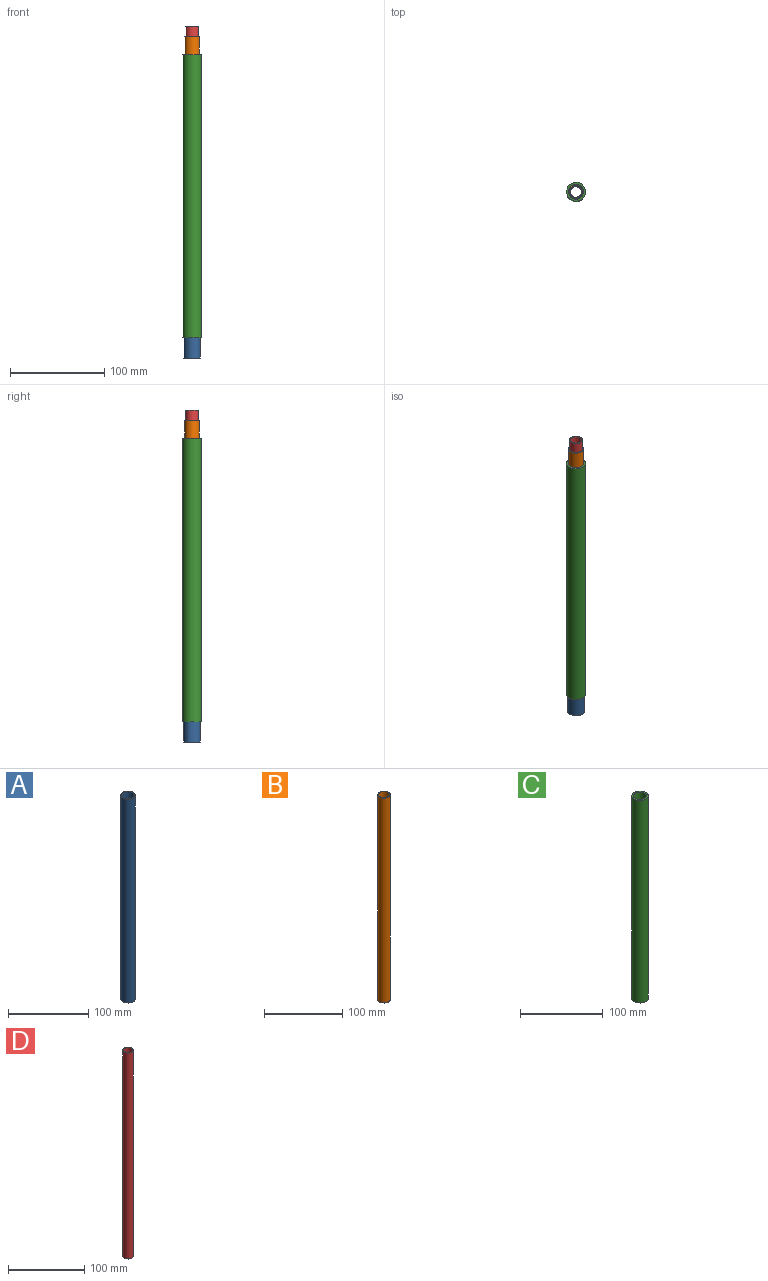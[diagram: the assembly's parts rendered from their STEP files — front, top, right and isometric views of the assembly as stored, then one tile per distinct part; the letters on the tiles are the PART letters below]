
ASSEMBLY  parts=4 mates=3
PART A: 4 faces, bbox 17.9x17.9x310 mm
  f0: cylinder r=7.95mm len=310mm, axis (0,0,-1), area 15484.9mm2, adj f2,f3
  f1: cylinder r=8.95mm len=310mm, axis (0,0,-1), area 17432.7mm2, adj f2,f3
  f2: plane 17.9x17.9mm, normal (0,0,1), area 53.1mm2, adj f0,f1
  f3: plane 17.9x17.9mm, normal (0,0,-1), area 53.1mm2, adj f0,f1
PART B: 4 faces, bbox 15.8x15.8x320 mm
  f0: cylinder r=6.9mm len=320mm, axis (0,0,-1), area 13873.3mm2, adj f2,f3
  f1: cylinder r=7.9mm len=320mm, axis (0,0,-1), area 15883.9mm2, adj f2,f3
  f2: plane 15.8x15.8mm, normal (0,0,1), area 46.5mm2, adj f0,f1
  f3: plane 15.8x15.8mm, normal (0,0,-1), area 46.5mm2, adj f0,f1
PART C: 4 faces, bbox 20x20x300 mm
  f0: cylinder r=7.8mm len=300mm, axis (0,0,-1), area 14702.7mm2, adj f2,f3
  f1: cylinder r=10mm len=300mm, axis (0,0,-1), area 18849.6mm2, adj f2,f3
  f2: plane 20x20mm, normal (0,0,1), area 123mm2, adj f0,f1
  f3: plane 20x20mm, normal (0,0,-1), area 123mm2, adj f0,f1
PART D: 4 faces, bbox 13.7x13.7x330 mm
  f0: cylinder r=5.85mm len=330mm, axis (0,0,-1), area 12129.7mm2, adj f2,f3
  f1: cylinder r=6.85mm len=330mm, axis (0,0,-1), area 14203.1mm2, adj f2,f3
  f2: plane 13.7x13.7mm, normal (0,0,1), area 39.9mm2, adj f0,f1
  f3: plane 13.7x13.7mm, normal (0,0,-1), area 39.9mm2, adj f0,f1
PLACE A t=(-68.41,10.72,-38.11)mm
PLACE B t=(-68.41,10.72,-17.8)mm
PLACE C t=(-68.41,10.72,-16.6)mm
PLACE D t=(-68.41,10.72,-16.18)mm
MATE cylindrical A.f0 <-> B.f0  axis (0,0,-1) through (-68.41,10.72,-38.11)mm
MATE cylindrical C.f1 <-> A.f0  axis (0,0,-1) through (-68.41,10.72,-16.6)mm
MATE cylindrical B.f0 <-> D.f0  axis (0,0,-1) through (-68.41,10.72,-17.8)mm
